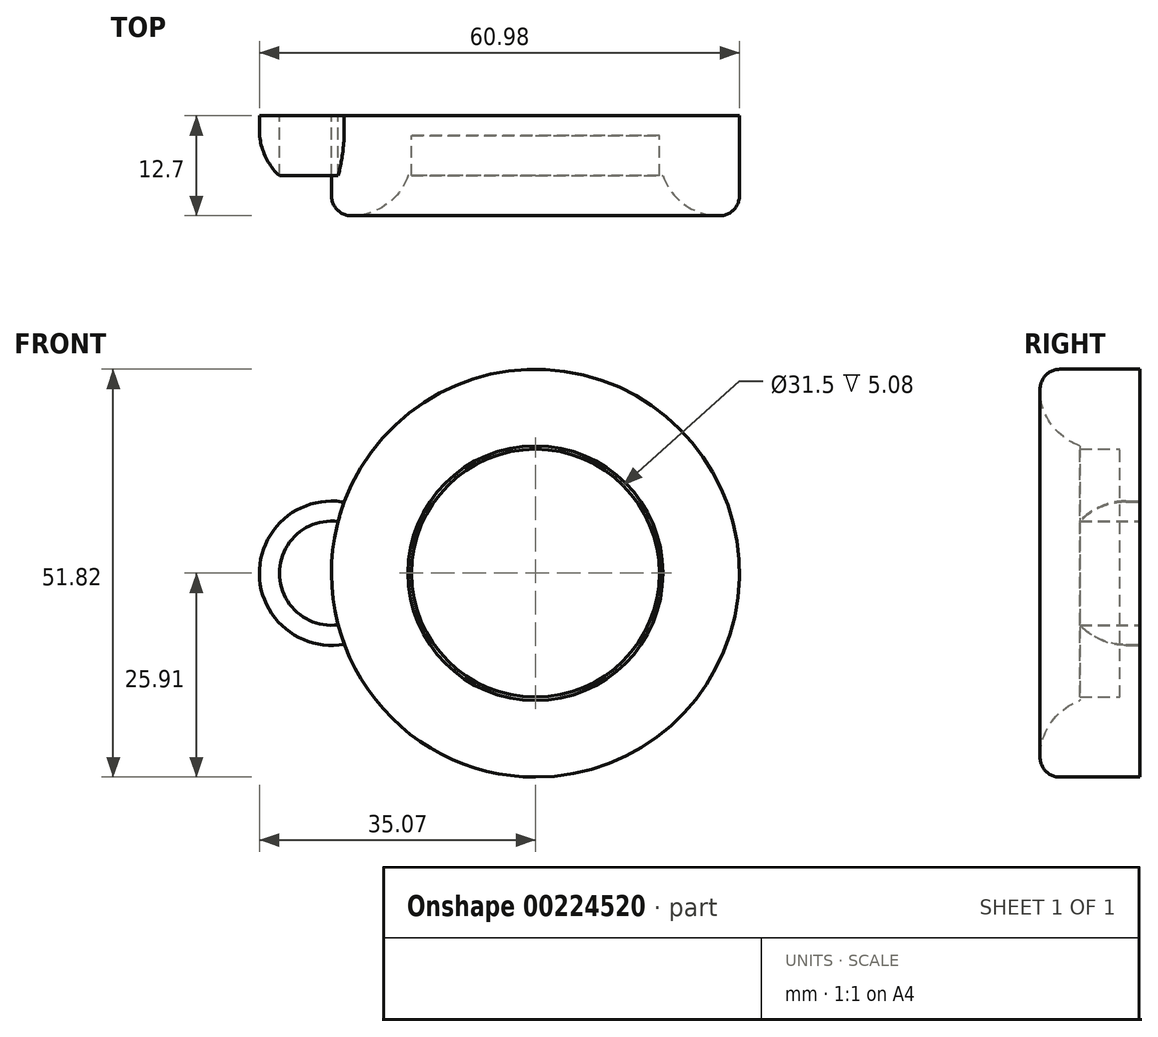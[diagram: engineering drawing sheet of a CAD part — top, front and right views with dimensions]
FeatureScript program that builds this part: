
annotation { "Feature Type Name" : "Feature", "Feature Type Description" : "" }
export const myFeature = defineFeature(function(context is Context, id is Id, definition is map)
    precondition{}
    {
        {
            var Q0;
            Q0=qCreatedBy(makeId("Front.planeOp"),FACE);
            var sketch = newSketch(context, id + "F0", { "sketchPlane" : qUnion([Q0])});
            skCircle(sketch, "E0", {"center": v(0, 0) * mm, "radius": 25.9 * mm});
            skCircle(sketch, "E1", {"center": v(0, 0) * mm, "radius": 15.75 * mm});
            skLineSegment(sketch, "E2", {"start": v(-15.75, 0) * mm, "end": v(15.75, 0) * mm});
            skLineSegment(sketch, "E3", {"start": v(-15.75, 0) * mm, "end": v(-25.9, 0) * mm});
            skArc(sketch, "E4", {"start": v(-25.06, 6.56) * mm, "mid": v(-32.52, 0) * mm, "end": v(-25.06, -6.56) * mm});
            skArc(sketch, "E5", {"start": v(-24.29, 9.02) * mm, "mid": v(-35.07, 0) * mm, "end": v(-24.29, -9.02) * mm});
            skSolve(sketch);
        }
        {
            var Q0;
            Q0=makeQuery(id+"F0.imprint","IMPRINT",FACE,{"disambiguationData":[TD([[makeQuery(id+"F0.imprint","IMPRINT",EDGE,{"derivedFrom":sQuery(id+"F0.wireOp",EDGE,"E0")}),1.0]])]});
            extrude(context, id + "F1", {"entities" : qUnion([Q0]), "depth" : 12.7 * mm});
        }
        {
            var Q0;
            {var subQ0=sQuery(id+"F0.wireOp",EDGE,"E2");Q0=makeQuery(id+"F0.imprint","IMPRINT",FACE,{"disambiguationData":[TD([[makeQuery(id+"F0.imprint","IMPRINT",EDGE,{"derivedFrom":subQ0}),1.0]])]});}
            var Q1;
            {var subQ0=sQuery(id+"F0.wireOp",EDGE,"E2");Q1=makeQuery(id+"F0.imprint","IMPRINT",FACE,{"disambiguationData":[TD([[makeQuery(id+"F0.imprint","IMPRINT",EDGE,{"derivedFrom":subQ0}),-1.0]])]});}
            extrude(context, id + "F2", {"entities" : qUnion([Q0, Q1]), "operationType" : NewBodyOperationType.ADD, "depth" : 2.54 * mm});
        }
        {
            var Q0;
            Q0=makeQuery(id+"F1.opExtrude","CAP_EDGE",EDGE,{"disambiguationData":[OSD([sQuery(id+"F0.wireOp",EDGE,"E1")])],"isStart":false});
            fillet(context, id + "F3", {"entities" : qUnion([Q0]), "radius" : 7.62 * mm, "tangentPropagation" : true, "allowEdgeOverflow" : false});
        }
        {
            var Q0;
            Q0=makeQuery(id+"F1.opExtrude","CAP_EDGE",EDGE,{"disambiguationData":[OSD([sQuery(id+"F0.wireOp",EDGE,"E0")])],"isStart":false});
            fillet(context, id + "F4", {"entities" : qUnion([Q0]), "radius" : 2.54 * mm, "tangentPropagation" : true, "allowEdgeOverflow" : false});
        }
        {
            var Q0;
            Q0 = qSketchRegion(id + "F0", true);
            extrude(context, id + "F5", {"entities" : qUnion([Q0]), "operationType" : NewBodyOperationType.ADD, "depth" : 7.62 * mm});
        }
        {
            var Q0;
            Q0=makeQuery(id+"F5.opExtrude","CAP_EDGE",EDGE,{"disambiguationData":[OSD([sQuery(id+"F0.wireOp",EDGE,"E5")])],"isStart":false});
            fillet(context, id + "F6", {"entities" : qUnion([Q0]), "radius" : 7.97 * mm, "tangentPropagation" : true, "allowEdgeOverflow" : false});
        }
    });
